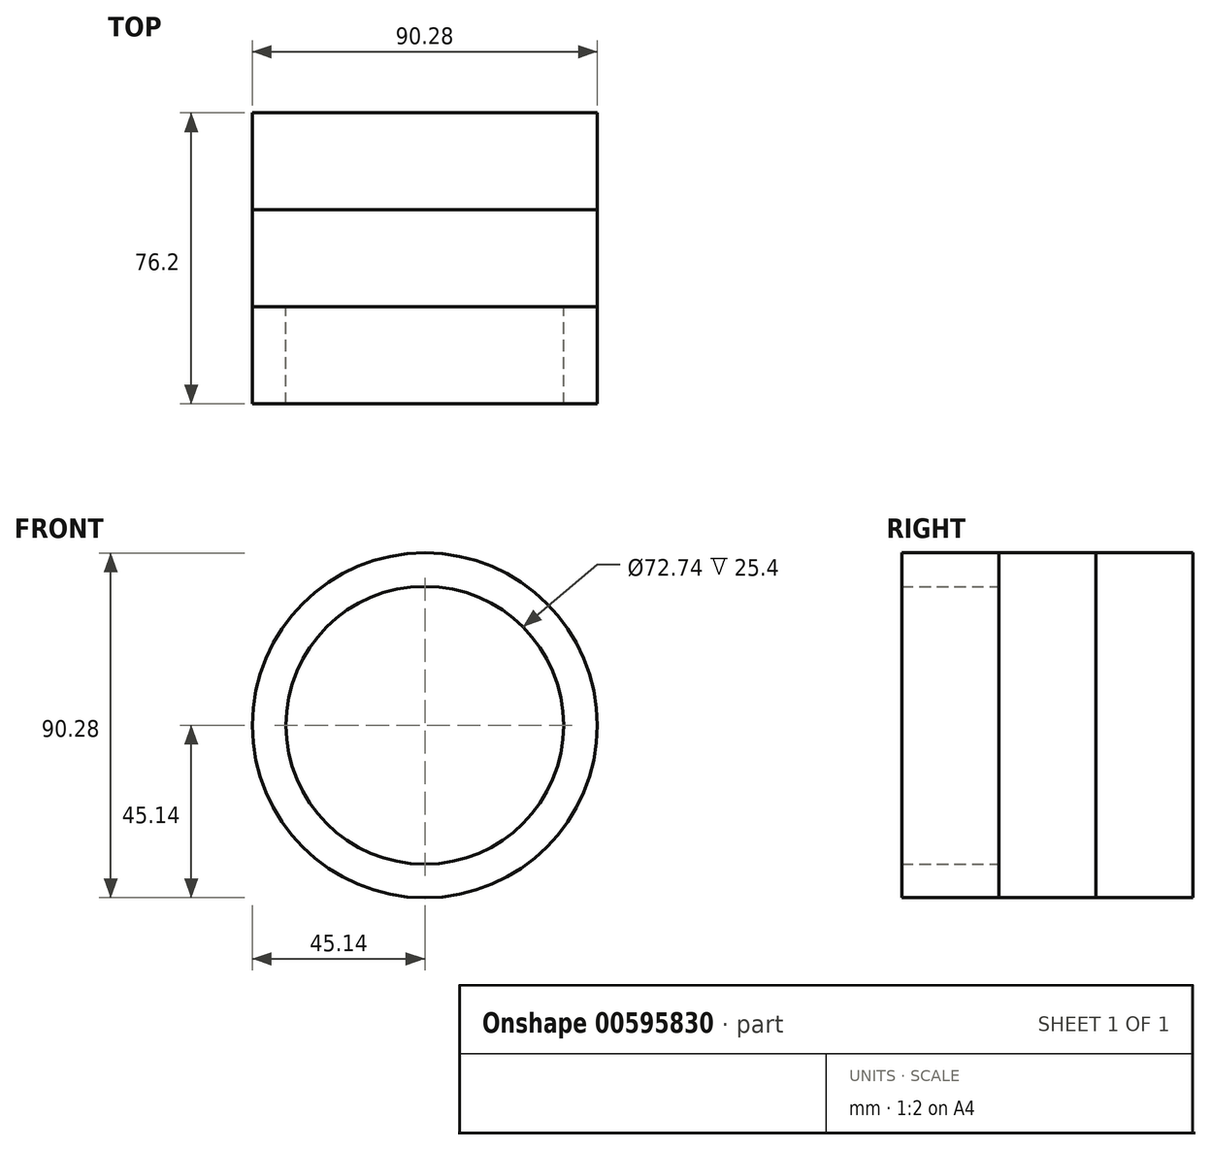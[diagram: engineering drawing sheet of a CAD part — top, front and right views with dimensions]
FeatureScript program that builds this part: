
annotation { "Feature Type Name" : "Feature", "Feature Type Description" : "" }
export const myFeature = defineFeature(function(context is Context, id is Id, definition is map)
    precondition{}
    {
        {
            var Q0;
            Q0=qCreatedBy(makeId("Front.planeOp"),FACE);
            var sketch = newSketch(context, id + "F0", { "sketchPlane" : qUnion([Q0])});
            skCircle(sketch, "E0", {"center": v(0, 0) * mm, "radius": 36.37 * mm});
            skCircle(sketch, "E1", {"center": v(0, 0) * mm, "radius": 45.14 * mm});
            skLineSegment(sketch, "E2", {"start": v(-9.35, 54.22) * mm, "end": v(0, 49.84) * mm});
            skLineSegment(sketch, "E3", {"start": v(0, 49.84) * mm, "end": v(8.19, 53.67) * mm});
            skLineSegment(sketch, "E4", {"start": v(8.19, 53.67) * mm, "end": v(15.43, 47.05) * mm});
            skLineSegment(sketch, "E5", {"start": v(15.43, 47.05) * mm, "end": v(24.32, 49.84) * mm});
            skLineSegment(sketch, "E6", {"start": v(24.32, 49.84) * mm, "end": v(27.3, 44.35) * mm});
            skLineSegment(sketch, "E7", {"start": v(27.3, 44.35) * mm, "end": v(36.7, 44.07) * mm});
            skLineSegment(sketch, "E8", {"start": v(36.7, 44.07) * mm, "end": v(38.53, 35.55) * mm});
            skLineSegment(sketch, "E9", {"start": v(38.53, 35.55) * mm, "end": v(47.31, 32.91) * mm});
            skLineSegment(sketch, "E10", {"start": v(47.31, 32.91) * mm, "end": v(44.75, 24.4) * mm});
            skLineSegment(sketch, "E11", {"start": v(44.75, 24.4) * mm, "end": v(52.3, 19.35) * mm});
            skLineSegment(sketch, "E12", {"start": v(52.3, 19.35) * mm, "end": v(47.31, 11.87) * mm});
            skSolve(sketch);
        }
        {
            var Q0;
            Q0 = qSketchRegion(id + "F0", true);
            var Q1;
            Q1=makeQuery(id+"F0.imprint","IMPRINT",FACE,{"disambiguationData":[TD([[makeQuery(id+"F0.imprint","IMPRINT",EDGE,{"derivedFrom":sQuery(id+"F0.wireOp",EDGE,"E0")}),1.0]])]});
            extrude(context, id + "F1", {"entities" : qUnion([Q0, Q1]), "depth" : 25.4 * mm, "offsetDistance" : 25.4 * mm});
        }
        {
            var Q0;
            Q0=makeQuery(id+"F0.imprint","IMPRINT",FACE,{"disambiguationData":[TD([[makeQuery(id+"F0.imprint","IMPRINT",EDGE,{"derivedFrom":sQuery(id+"F0.wireOp",EDGE,"E0")}),-1.0]])]});
            extrude(context, id + "F2", {"entities" : qUnion([Q0]), "depth" : 25.4 * mm, "offsetDistance" : 25.4 * mm});
        }
        {
            var Q0;
            Q0=makeQuery(id+"F1.opExtrude","CAP_FACE",FACE,{"disambiguationData":[OSD([sQuery(id+"F0.wireOp",EDGE,"E1")])],"isStart":true});
            var Q1;
            Q1=makeQuery(id+"F1.opExtrude","CAP_FACE",FACE,{"disambiguationData":[OSD([sQuery(id+"F0.wireOp",EDGE,"E1")])],"isStart":false});
            extrude(context, id + "F3", {"entities" : qUnion([Q0, Q1]), "depth" : 50.8 * mm, "offsetDistance" : 25.4 * mm});
        }
    });
